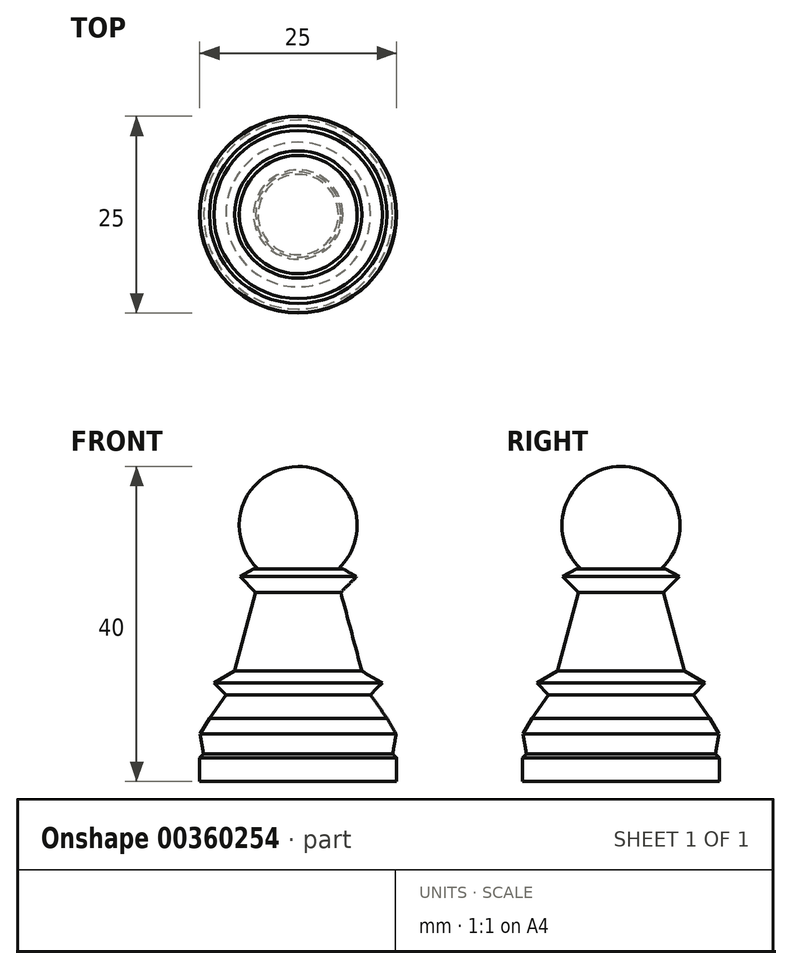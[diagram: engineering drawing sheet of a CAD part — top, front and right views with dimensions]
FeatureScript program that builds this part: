
annotation { "Feature Type Name" : "Feature", "Feature Type Description" : "" }
export const myFeature = defineFeature(function(context is Context, id is Id, definition is map)
    precondition{}
    {
        {
            var Q0;
            Q0=qCreatedBy(makeId("Top.planeOp"),FACE);
            var sketch = newSketch(context, id + "F0", { "sketchPlane" : qUnion([Q0])});
            skCircle(sketch, "E0", {"center": v(0, 0) * mm, "radius": 12.5 * mm});
            skSolve(sketch);
        }
        {
            var Q0;
            Q0=makeQuery(id+"F0.imprint","IMPRINT",FACE,{"disambiguationData":[TD([[makeQuery(id+"F0.imprint","IMPRINT",EDGE,{"derivedFrom":sQuery(id+"F0.wireOp",EDGE,"E0")}),1.0]])]});
            extrude(context, id + "F1", {"entities" : qUnion([Q0]), "depth" : 3 * mm});
        }
        {
            var Q0;
            Q0=makeQuery(id+"F1.opExtrude","CAP_FACE",FACE,{"disambiguationData":[OSD([sQuery(id+"F0.wireOp",EDGE,"E0")])],"isStart":false});
            extrude(context, id + "F2", {"entities" : qUnion([Q0]), "operationType" : NewBodyOperationType.ADD, "depth" : 0.5 * mm, "hasDraft" : true, "draftAngle" : 45 * degree, "draftPullDirection" : true});
        }
        {
            var Q0;
            Q0=makeQuery(id+"F2.opExtrude","CAP_FACE",FACE,{"disambiguationData":[OSD([sQuery(id+"F0.wireOp",EDGE,"E0")])],"isStart":false});
            extrude(context, id + "F3", {"entities" : qUnion([Q0]), "operationType" : NewBodyOperationType.ADD, "depth" : 2.5 * mm, "hasDraft" : true, "draftAngle" : 10 * degree});
        }
        {
            var Q0;
            Q0=makeQuery(id+"F3.opExtrude","CAP_FACE",FACE,{"disambiguationData":[OSD([sQuery(id+"F0.wireOp",EDGE,"E0")])],"isStart":false});
            extrude(context, id + "F4", {"entities" : qUnion([Q0]), "operationType" : NewBodyOperationType.ADD, "depth" : 2 * mm, "hasDraft" : true, "draftAngle" : 30 * degree, "draftPullDirection" : true});
        }
        {
            var Q0;
            Q0=makeQuery(id+"F4.opExtrude","CAP_FACE",FACE,{"disambiguationData":[OSD([sQuery(id+"F0.wireOp",EDGE,"E0")])],"isStart":false});
            extrude(context, id + "F5", {"entities" : qUnion([Q0]), "operationType" : NewBodyOperationType.ADD, "depth" : 3 * mm, "hasDraft" : true, "draftAngle" : 35 * degree, "draftPullDirection" : true});
        }
        {
            var Q0;
            Q0=makeQuery(id+"F5.opExtrude","CAP_FACE",FACE,{"disambiguationData":[OSD([sQuery(id+"F0.wireOp",EDGE,"E0")])],"isStart":false});
            extrude(context, id + "F6", {"entities" : qUnion([Q0]), "operationType" : NewBodyOperationType.ADD, "depth" : 1.5 * mm, "hasDraft" : true, "draftAngle" : 45 * degree});
        }
        {
            var Q0;
            Q0=makeQuery(id+"F6.opExtrude","CAP_FACE",FACE,{"disambiguationData":[OSD([sQuery(id+"F0.wireOp",EDGE,"E0")])],"isStart":false});
            extrude(context, id + "F7", {"entities" : qUnion([Q0]), "operationType" : NewBodyOperationType.ADD, "depth" : 1.5 * mm, "hasDraft" : true, "draftAngle" : 60 * degree, "draftPullDirection" : true});
        }
        {
            var Q0;
            Q0=makeQuery(id+"F7.opExtrude","CAP_FACE",FACE,{"disambiguationData":[OSD([sQuery(id+"F0.wireOp",EDGE,"E0")])],"isStart":false});
            extrude(context, id + "F8", {"entities" : qUnion([Q0]), "operationType" : NewBodyOperationType.ADD, "depth" : 10 * mm, "hasDraft" : true, "draftAngle" : 15 * degree, "draftPullDirection" : true});
        }
        {
            var Q0;
            Q0=makeQuery(id+"F8.opExtrude","CAP_FACE",FACE,{"disambiguationData":[OSD([sQuery(id+"F0.wireOp",EDGE,"E0")])],"isStart":false});
            extrude(context, id + "F9", {"entities" : qUnion([Q0]), "operationType" : NewBodyOperationType.ADD, "depth" : 2 * mm, "hasDraft" : true, "draftAngle" : 45 * degree});
        }
        {
            var Q0;
            Q0=makeQuery(id+"F9.opExtrude","CAP_FACE",FACE,{"disambiguationData":[OSD([sQuery(id+"F0.wireOp",EDGE,"E0")])],"isStart":false});
            extrude(context, id + "F10", {"entities" : qUnion([Q0]), "operationType" : NewBodyOperationType.ADD, "depth" : 1 * mm, "hasDraft" : true, "draftAngle" : 60 * degree, "draftPullDirection" : true});
        }
        {
            var Q0;
            Q0=qCreatedBy(makeId("Front.planeOp"),FACE);
            var sketch = newSketch(context, id + "F11", { "sketchPlane" : qUnion([Q0])});
            skCircle(sketch, "E1", {"center": v(0, 32.5) * mm, "radius": 7.5 * mm});
            skLineSegment(sketch, "E2", {"start": v(0, 0) * mm, "end": v(0, 40) * mm});
            skSolve(sketch);
        }
        {
            var Q0;
            {var subQ0=sQuery(id+"F11.wireOp",EDGE,"E2");var subQ1=sQuery(id+"F11.wireOp",EDGE,"E1");var subQ2=makeQuery(id+"F11.imprint","INTERSECT",VERTEX,{"disambiguationData":[OD(0.0)],"derivedFrom":[subQ1,subQ0]});Q0=makeQuery(id+"F11.imprint","IMPRINT",FACE,{"disambiguationData":[TD([[makeQuery(id+"F11.imprint","IMPRINT",EDGE,{"disambiguationData":[TD([[subQ2,-1.0]])],"derivedFrom":subQ1}),1.0]])]});}
            var Q1;
            Q1=sQuery(id+"F11.wireOp",EDGE,"E2");
            revolve(context, id + "F12", {"operationType" : NewBodyOperationType.ADD, "entities" : qUnion([Q0]), "axis" : qUnion([Q1]), "revolveType" : RevolveType.FULL});
        }
    });
